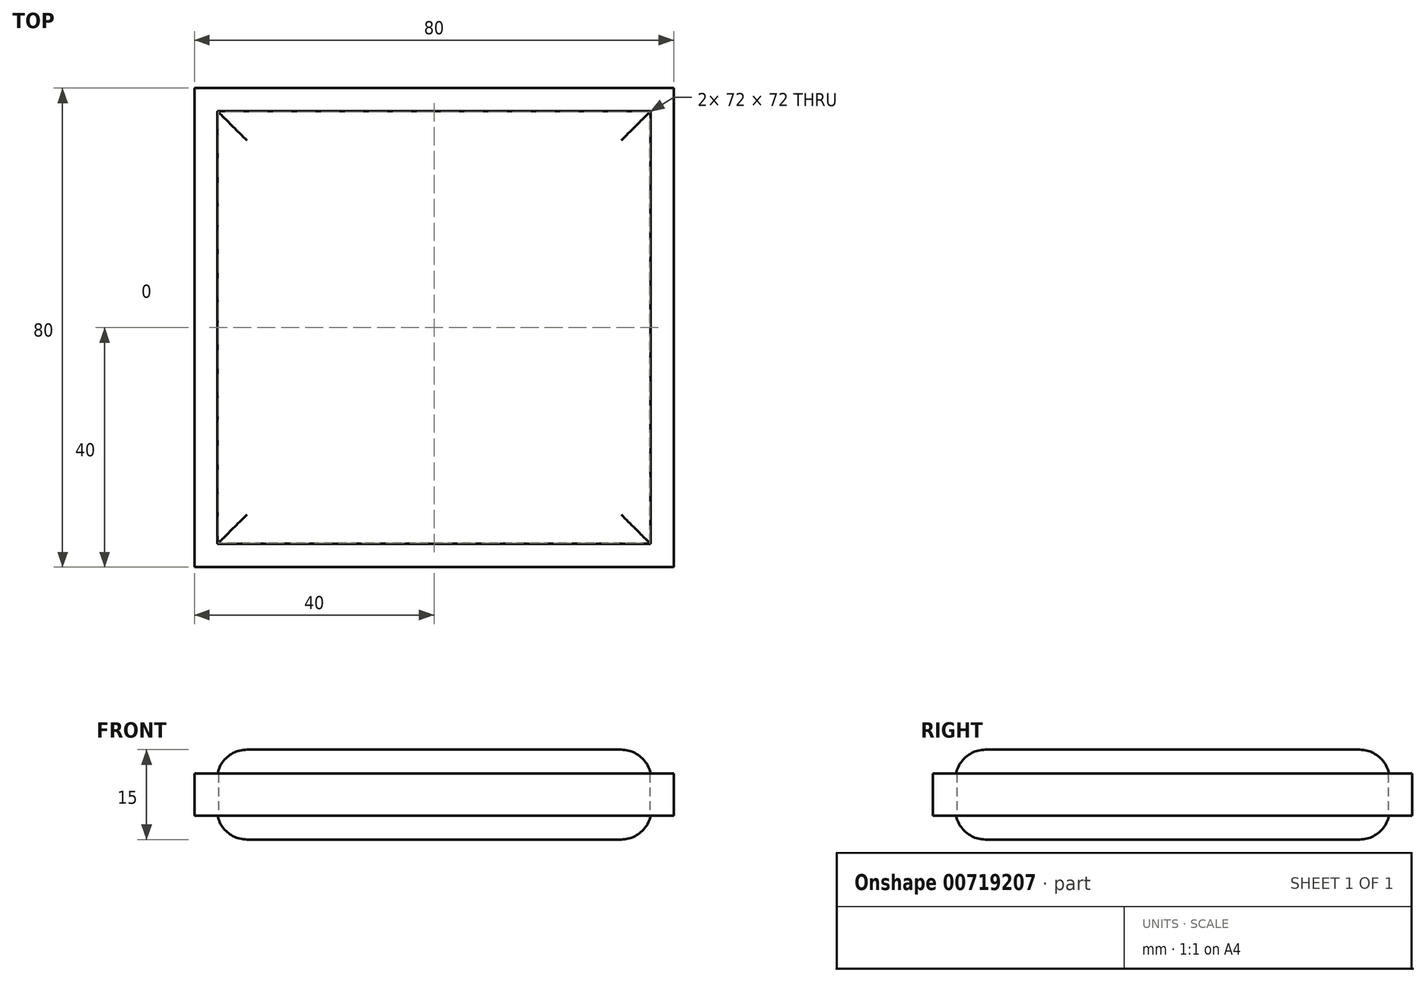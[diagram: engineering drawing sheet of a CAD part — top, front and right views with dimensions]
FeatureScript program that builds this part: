
annotation { "Feature Type Name" : "Feature", "Feature Type Description" : "" }
export const myFeature = defineFeature(function(context is Context, id is Id, definition is map)
    precondition{}
    {
        {
            assignVariable(context, id + "F0", {"name" : "depth", "anyValue" : 7 * mm});
        }
        {
            assignVariable(context, id + "F1", {"name" : "height", "anyValue" : 15 * mm});
        }
        {
            var Q0;
            Q0=qCreatedBy(makeId("Top.planeOp"),FACE);
            var sketch = newSketch(context, id + "F2", { "sketchPlane" : qUnion([Q0])});
            skLineSegment(sketch, "E0.bottom", {"start": v(40, -40) * mm, "end": v(-40, -40) * mm});
            skLineSegment(sketch, "E0.top", {"start": v(40, 40) * mm, "end": v(-40, 40) * mm});
            skLineSegment(sketch, "E0.left", {"start": v(40, -40) * mm, "end": v(40, 40) * mm});
            skLineSegment(sketch, "E0.right", {"start": v(-40, -40) * mm, "end": v(-40, 40) * mm});
            skPoint(sketch, "E0.middle", {"position": v(0, 0) * mm});
            skLineSegment(sketch, "E1.bottom", {"start": v(36, -36) * mm, "end": v(-36, -36) * mm});
            skLineSegment(sketch, "E1.top", {"start": v(36, 36) * mm, "end": v(-36, 36) * mm});
            skLineSegment(sketch, "E1.left", {"start": v(36, -36) * mm, "end": v(36, 36) * mm});
            skLineSegment(sketch, "E1.right", {"start": v(-36, -36) * mm, "end": v(-36, 36) * mm});
            skSolve(sketch);
        }
        {
            var Q0;
            Q0=makeQuery(id+"F2.imprint","IMPRINT",FACE,{"disambiguationData":[TD([[makeQuery(id+"F2.imprint","IMPRINT",EDGE,{"derivedFrom":sQuery(id+"F2.wireOp",EDGE,"E0.bottom")}),-1.0]])]});
            extrude(context, id + "F3", {"entities" : qUnion([Q0]), "endBound" : BoundingType.SYMMETRIC, "depth" : getVariable(context, 'depth'), "offsetDistance" : 25 * mm});
        }
        {
            var Q0;
            Q0=qCreatedBy(makeId("Top.planeOp"),FACE);
            var sketch = newSketch(context, id + "F4", { "sketchPlane" : qUnion([Q0])});
            skLineSegment(sketch, "E2.bottom", {"start": v(36.25, -36.25) * mm, "end": v(-36.25, -36.25) * mm});
            skLineSegment(sketch, "E2.top", {"start": v(36.25, 36.25) * mm, "end": v(-36.25, 36.25) * mm});
            skLineSegment(sketch, "E2.left", {"start": v(36.25, -36.25) * mm, "end": v(36.25, 36.25) * mm});
            skLineSegment(sketch, "E2.right", {"start": v(-36.25, -36.25) * mm, "end": v(-36.25, 36.25) * mm});
            skPoint(sketch, "E2.middle", {"position": v(0, 0) * mm});
            skSolve(sketch);
        }
        {
            var Q0;
            Q0=qSketchRegion(id+"F4",true);
            extrude(context, id + "F5", {"entities" : qUnion([Q0]), "endBound" : BoundingType.SYMMETRIC, "depth" : getVariable(context, 'height'), "offsetDistance" : 25 * mm});
        }
        {
            var Q0;
            Q0=makeQuery(id+"F5.opExtrude","CAP_FACE",FACE,{"disambiguationData":[OSD([sQuery(id+"F4.wireOp",EDGE,"E2.bottom"),sQuery(id+"F4.wireOp",EDGE,"E2.top"),sQuery(id+"F4.wireOp",EDGE,"E2.left"),sQuery(id+"F4.wireOp",EDGE,"E2.right")])],"isStart":false});
            var Q1;
            Q1=makeQuery(id+"F5.opExtrude","CAP_FACE",FACE,{"disambiguationData":[OSD([sQuery(id+"F4.wireOp",EDGE,"E2.bottom"),sQuery(id+"F4.wireOp",EDGE,"E2.top"),sQuery(id+"F4.wireOp",EDGE,"E2.left"),sQuery(id+"F4.wireOp",EDGE,"E2.right")])],"isStart":true});
            fillet(context, id + "F6", {"entities" : qUnion([Q0, Q1]), "radius" : 5 * mm, "tangentPropagation" : true, "allowEdgeOverflow" : false});
        }
        {
            var Q0;
            Q0=makeQuery(id+"F3.opExtrude","SWEPT_BODY",BODY,{"disambiguationData":[OSD([sQuery(id+"F2.wireOp",EDGE,"E0.bottom"),sQuery(id+"F2.wireOp",EDGE,"E0.top"),sQuery(id+"F2.wireOp",EDGE,"E0.left"),sQuery(id+"F2.wireOp",EDGE,"E0.right"),sQuery(id+"F2.wireOp",EDGE,"E1.bottom"),sQuery(id+"F2.wireOp",EDGE,"E1.top"),sQuery(id+"F2.wireOp",EDGE,"E1.left"),sQuery(id+"F2.wireOp",EDGE,"E1.right")])]});
            transform(context, id + "F7", {"entities" : qUnion([Q0]), "transformType" : TransformType.TRANSLATION_3D, "dx" : 0 * mm, "dy" : 0 * mm, "dz" : 0 * mm, "makeCopy" : true});
        }
        {
            var Q0;
            Q0=makeQuery(id+"F7.opPattern","COPY",BODY,{"derivedFrom":makeQuery(id+"F3.opExtrude","SWEPT_BODY",BODY,{"disambiguationData":[OSD([sQuery(id+"F2.wireOp",EDGE,"E0.bottom"),sQuery(id+"F2.wireOp",EDGE,"E0.top"),sQuery(id+"F2.wireOp",EDGE,"E0.left"),sQuery(id+"F2.wireOp",EDGE,"E0.right"),sQuery(id+"F2.wireOp",EDGE,"E1.bottom"),sQuery(id+"F2.wireOp",EDGE,"E1.top"),sQuery(id+"F2.wireOp",EDGE,"E1.left"),sQuery(id+"F2.wireOp",EDGE,"E1.right")])]}),"instanceName":"1"});
            var Q1;
            Q1=makeQuery(id+"F5.opExtrude","SWEPT_BODY",BODY,{"disambiguationData":[OSD([sQuery(id+"F4.wireOp",EDGE,"E2.bottom"),sQuery(id+"F4.wireOp",EDGE,"E2.top"),sQuery(id+"F4.wireOp",EDGE,"E2.left"),sQuery(id+"F4.wireOp",EDGE,"E2.right")])]});
            booleanBodies(context, id + "F8", {"operationType" : BooleanOperationType.SUBTRACTION, "tools" : qUnion([Q0]), "targets" : qUnion([Q1])});
        }
    });
